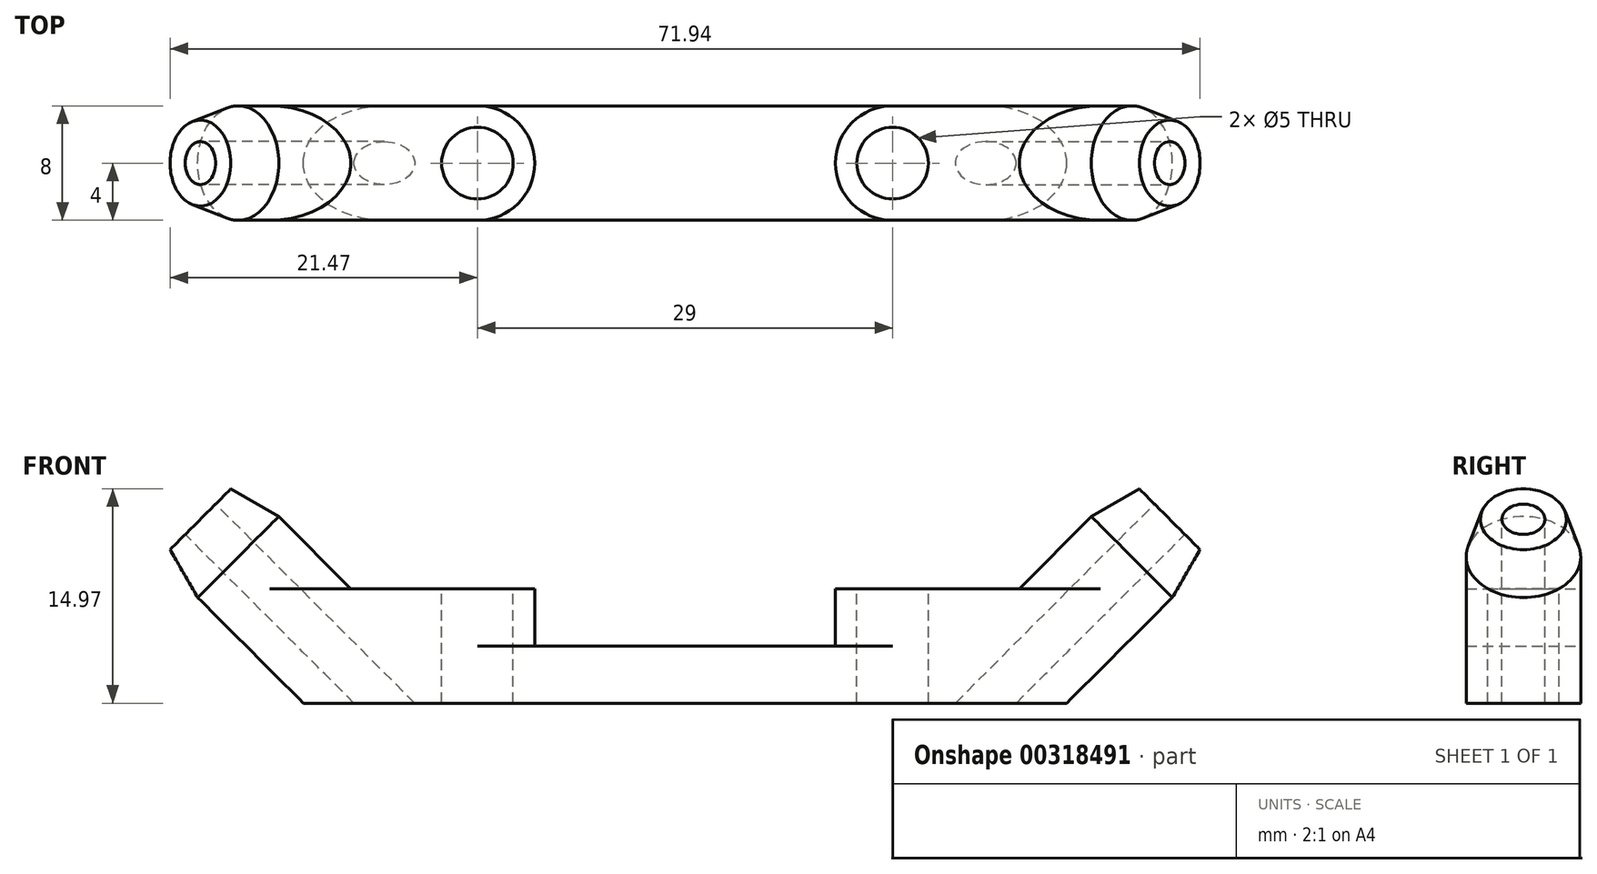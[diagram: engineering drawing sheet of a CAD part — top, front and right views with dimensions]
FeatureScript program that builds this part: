
annotation { "Feature Type Name" : "Feature", "Feature Type Description" : "" }
export const myFeature = defineFeature(function(context is Context, id is Id, definition is map)
    precondition{}
    {
        {
            var Q0;
            Q0=qCreatedBy(makeId("Front.planeOp"),FACE);
            var sketch = newSketch(context, id + "F0", { "sketchPlane" : qUnion([Q0])});
            skLineSegment(sketch, "E0", {"start": v(0, 0) * mm, "end": v(-26.66, 0) * mm});
            skLineSegment(sketch, "E1", {"start": v(-26.66, 0) * mm, "end": v(-34.66, 8) * mm});
            skLineSegment(sketch, "E2", {"start": v(-34.66, 8) * mm, "end": v(0, 8) * mm});
            skLineSegment(sketch, "E3", {"start": v(0, 8) * mm, "end": v(0, 0) * mm});
            skLineSegment(sketch, "E4", {"start": v(-29, 8) * mm, "end": v(-21, 0) * mm, "construction": true});
            skLineSegment(sketch, "E5", {"start": v(0, 8) * mm, "end": v(0, 31.76) * mm, "construction": true});
            skSolve(sketch);
        }
        {
            var Q0;
            Q0 = qSketchRegion(id + "F0", true);
            extrude(context, id + "F1", {"entities" : qUnion([Q0]), "endBound" : BoundingType.SYMMETRIC, "depth" : 8 * mm});
        }
        {
            var Q0;
            Q0=makeQuery(id+"F1.opExtrude","CAP_EDGE",EDGE,{"disambiguationData":[OSD([sQuery(id+"F0.wireOp",EDGE,"E1")])],"isStart":true});
            var Q1;
            Q1=makeQuery(id+"F1.opExtrude","CAP_EDGE",EDGE,{"disambiguationData":[OSD([sQuery(id+"F0.wireOp",EDGE,"E1")])],"isStart":false});
            fillet(context, id + "F2", {"entities" : qUnion([Q0, Q1]), "radius" : 4 * mm, "tangentPropagation" : true, "allowEdgeOverflow" : false});
        }
        {
            var Q0;
            Q0=makeQuery(id+"F1.opExtrude","SWEPT_FACE",FACE,{"disambiguationData":[OSD([sQuery(id+"F0.wireOp",EDGE,"E2")])]});
            var sketch = newSketch(context, id + "F3", { "sketchPlane" : qUnion([Q0])});
            skCircle(sketch, "E6", {"center": v(-14.5, 0) * mm, "radius": 2.5 * mm});
            skLineSegment(sketch, "E7", {"start": v(-14.5, 0) * mm, "end": v(0, 0) * mm, "construction": true});
            skLineSegment(sketch, "E8", {"start": v(0, 0) * mm, "end": v(0, 20.84) * mm, "construction": true});
            skSolve(sketch);
        }
        {
            var Q0;
            Q0 = qSketchRegion(id + "F3", true);
            extrude(context, id + "F4", {"entities" : qUnion([Q0]), "operationType" : NewBodyOperationType.REMOVE, "endBound" : BoundingType.UP_TO_NEXT, "oppositeDirection" : true, "depth" : 25.4 * mm});
        }
        {
            var Q0;
            Q0=makeQuery(id+"F1.opExtrude","SWEPT_FACE",FACE,{"disambiguationData":[OSD([sQuery(id+"F0.wireOp",EDGE,"E2")])]});
            var sketch = newSketch(context, id + "F5", { "sketchPlane" : qUnion([Q0])});
            skArc(sketch, "E9", {"start": v(-14.5, -4) * mm, "mid": v(-10.5, 0) * mm, "end": v(-14.5, 4) * mm});
            skLineSegment(sketch, "E10", {"start": v(-14.5, 4) * mm, "end": v(0, 4) * mm});
            skLineSegment(sketch, "E11", {"start": v(0, 4) * mm, "end": v(0, -4) * mm});
            skLineSegment(sketch, "E12", {"start": v(0, -4) * mm, "end": v(-14.5, -4) * mm});
            skLineSegment(sketch, "E13", {"start": v(-14.5, -4) * mm, "end": v(-14.5, 4) * mm, "construction": true});
            skPoint(sketch, "E14", {"position": v(-14.5, 4) * mm});
            skSolve(sketch);
        }
        {
            var Q0;
            Q0 = qSketchRegion(id + "F5", true);
            extrude(context, id + "F6", {"entities" : qUnion([Q0]), "operationType" : NewBodyOperationType.REMOVE, "oppositeDirection" : true, "depth" : 4 * mm});
        }
        {
            var Q0;
            Q0=qCreatedBy(makeId("Front.planeOp"),FACE);
            var sketch = newSketch(context, id + "F7", { "sketchPlane" : qUnion([Q0])});
            skLineSegment(sketch, "E15", {"start": v(-19.45, -1.55) * mm, "end": v(-43.54, 22.54) * mm});
            skLineSegment(sketch, "E16", {"start": v(-43.54, 22.54) * mm, "end": v(-44.6, 21.48) * mm});
            skLineSegment(sketch, "E17", {"start": v(-44.6, 21.48) * mm, "end": v(-20.51, -2.61) * mm});
            skLineSegment(sketch, "E18", {"start": v(-20.51, -2.61) * mm, "end": v(-19.45, -1.55) * mm});
            skLineSegment(sketch, "E19", {"start": v(-37.85, 16.85) * mm, "end": v(-43.54, 22.54) * mm, "construction": true});
            skSolve(sketch);
        }
        {
            var Q0;
            Q0=sQuery(id+"F0.wireOp",EDGE,"E4");
            var Q1;
            Q1=sQuery(id+"F0.wireOp",VERTEX,"E4.start");
            cPlane(context, id + "F8", {"entities" : qUnion([Q0, Q1]), "cplaneType" : CPlaneType.LINE_POINT, "offset" : 25 * mm, "width" : 150 * mm, "height" : 150 * mm});
        }
        {
            var Q0;
            Q0=qCreatedBy(id+"F8.planeOp",FACE);
            var sketch = newSketch(context, id + "F9", { "sketchPlane" : qUnion([Q0])});
            skCircle(sketch, "E20", {"center": v(0, -14.85) * mm, "radius": 4 * mm});
            skSolve(sketch);
        }
        {
            var Q0;
            Q0 = qSketchRegion(id + "F9", true);
            extrude(context, id + "F10", {"entities" : qUnion([Q0]), "operationType" : NewBodyOperationType.ADD, "endBound" : BoundingType.SYMMETRIC, "oppositeDirection" : true, "depth" : 13.7 * mm});
        }
        {
            var Q0;
            Q0 = qSketchRegion(id + "F7", true);
            var Q1;
            Q1=sQuery(id+"F7.wireOp",EDGE,"E15");
            revolve(context, id + "F11", {"operationType" : NewBodyOperationType.REMOVE, "entities" : qUnion([Q0]), "axis" : qUnion([Q1]), "revolveType" : RevolveType.FULL, "oppositeDirection" : true});
        }
        {
            var Q0;
            Q0=makeQuery(id+"F10.opExtrude","CAP_EDGE",EDGE,{"disambiguationData":[OSD([sQuery(id+"F9.wireOp",EDGE,"E20")])],"isStart":false});
            chamfer(context, id + "F12", {"entities" : qUnion([Q0]), "chamferType" : ChamferType.OFFSET_ANGLE, "width" : 1 * mm, "oppositeDirection" : true, "angle" : 75 * degree, "tangentPropagation" : true});
        }
        {
            var Q0;
            Q0=makeQuery(id+"F1.opExtrude","SWEPT_BODY",BODY,{"disambiguationData":[OSD([sQuery(id+"F0.wireOp",EDGE,"E0"),sQuery(id+"F0.wireOp",EDGE,"E1"),sQuery(id+"F0.wireOp",EDGE,"E2"),sQuery(id+"F0.wireOp",EDGE,"E3")])]});
            var Q1;
            Q1=makeQuery(id+"F1.opExtrude","SWEPT_FACE",FACE,{"disambiguationData":[OSD([sQuery(id+"F0.wireOp",EDGE,"E3")])]});
            mirror(context, id + "F13", {"operationType" : NewBodyOperationType.ADD, "entities" : qUnion([Q0]), "mirrorPlane" : qUnion([Q1])});
        }
    });
